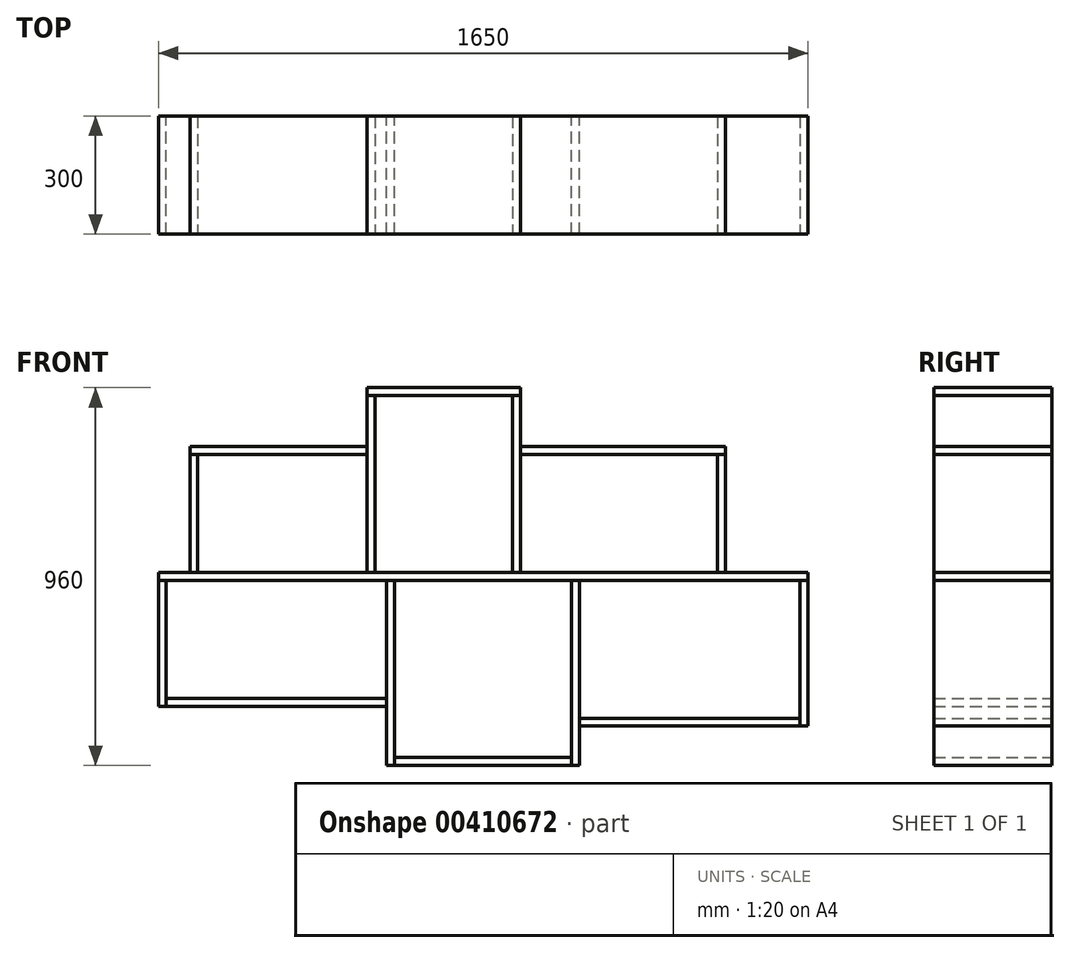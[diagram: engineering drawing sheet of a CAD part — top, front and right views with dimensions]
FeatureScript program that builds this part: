
annotation { "Feature Type Name" : "Feature", "Feature Type Description" : "" }
export const myFeature = defineFeature(function(context is Context, id is Id, definition is map)
    precondition{}
    {
        {
            var Q0;
            Q0=qCreatedBy(makeId("Top.planeOp"),FACE);
            var sketch = newSketch(context, id + "F0", { "sketchPlane" : qUnion([Q0])});
            skLineSegment(sketch, "E0.bottom", {"start": v(-825, 149.72) * mm, "end": v(825, 149.72) * mm});
            skLineSegment(sketch, "E0.top", {"start": v(-825, -150.28) * mm, "end": v(825, -150.28) * mm});
            skLineSegment(sketch, "E0.left", {"start": v(-825, 149.72) * mm, "end": v(-825, -150.28) * mm});
            skLineSegment(sketch, "E0.right", {"start": v(825, 149.72) * mm, "end": v(825, -150.28) * mm});
            skSolve(sketch);
        }
        {
            var Q0;
            Q0 = qSketchRegion(id + "F0", true);
            extrude(context, id + "F1", {"entities" : qUnion([Q0]), "depth" : 20 * mm});
        }
        {
            var Q0;
            Q0=makeQuery(id+"F1.opExtrude","CAP_FACE",FACE,{"disambiguationData":[OSD([sQuery(id+"F0.wireOp",EDGE,"E0.bottom"),sQuery(id+"F0.wireOp",EDGE,"E0.top"),sQuery(id+"F0.wireOp",EDGE,"E0.left"),sQuery(id+"F0.wireOp",EDGE,"E0.right")])],"isStart":false});
            var sketch = newSketch(context, id + "F2", { "sketchPlane" : qUnion([Q0])});
            skLineSegment(sketch, "E1.bottom", {"start": v(-725, 149.72) * mm, "end": v(-745, 149.72) * mm});
            skLineSegment(sketch, "E1.top", {"start": v(-725, -150.28) * mm, "end": v(-745, -150.28) * mm});
            skLineSegment(sketch, "E1.left", {"start": v(-745, 149.72) * mm, "end": v(-745, -150.28) * mm});
            skLineSegment(sketch, "E1.right", {"start": v(-725, 149.72) * mm, "end": v(-725, -150.28) * mm});
            skSolve(sketch);
        }
        {
            var Q0;
            Q0 = qSketchRegion(id + "F2", true);
            extrude(context, id + "F3", {"entities" : qUnion([Q0]), "depth" : 300 * mm});
        }
        {
            var Q0;
            Q0=makeQuery(id+"F1.opExtrude","CAP_FACE",FACE,{"disambiguationData":[OSD([sQuery(id+"F0.wireOp",EDGE,"E0.bottom"),sQuery(id+"F0.wireOp",EDGE,"E0.top"),sQuery(id+"F0.wireOp",EDGE,"E0.left"),sQuery(id+"F0.wireOp",EDGE,"E0.right")])],"isStart":false});
            var sketch = newSketch(context, id + "F4", { "sketchPlane" : qUnion([Q0])});
            skLineSegment(sketch, "E2.bottom", {"start": v(-295, 149.72) * mm, "end": v(-275, 149.72) * mm});
            skLineSegment(sketch, "E2.top", {"start": v(-295, -150.28) * mm, "end": v(-275, -150.28) * mm});
            skLineSegment(sketch, "E2.left", {"start": v(-295, 149.72) * mm, "end": v(-295, -150.28) * mm});
            skLineSegment(sketch, "E2.right", {"start": v(-275, 149.72) * mm, "end": v(-275, -150.28) * mm});
            skSolve(sketch);
        }
        {
            var Q0;
            Q0 = qSketchRegion(id + "F4", true);
            extrude(context, id + "F5", {"entities" : qUnion([Q0]), "depth" : 450 * mm});
        }
        {
            var Q0;
            Q0=makeQuery(id+"F1.opExtrude","CAP_FACE",FACE,{"disambiguationData":[OSD([sQuery(id+"F0.wireOp",EDGE,"E0.bottom"),sQuery(id+"F0.wireOp",EDGE,"E0.top"),sQuery(id+"F0.wireOp",EDGE,"E0.left"),sQuery(id+"F0.wireOp",EDGE,"E0.right")])],"isStart":false});
            var sketch = newSketch(context, id + "F6", { "sketchPlane" : qUnion([Q0])});
            skLineSegment(sketch, "E3.bottom", {"start": v(75, 149.72) * mm, "end": v(95, 149.72) * mm});
            skLineSegment(sketch, "E3.top", {"start": v(75, -150.28) * mm, "end": v(95, -150.28) * mm});
            skLineSegment(sketch, "E3.left", {"start": v(75, 149.72) * mm, "end": v(75, -150.28) * mm});
            skLineSegment(sketch, "E3.right", {"start": v(95, 149.72) * mm, "end": v(95, -150.28) * mm});
            skSolve(sketch);
        }
        {
            var Q0;
            Q0 = qSketchRegion(id + "F6", true);
            extrude(context, id + "F7", {"entities" : qUnion([Q0]), "depth" : 450 * mm});
        }
        {
            var Q0;
            Q0=makeQuery(id+"F1.opExtrude","CAP_FACE",FACE,{"disambiguationData":[OSD([sQuery(id+"F0.wireOp",EDGE,"E0.bottom"),sQuery(id+"F0.wireOp",EDGE,"E0.top"),sQuery(id+"F0.wireOp",EDGE,"E0.left"),sQuery(id+"F0.wireOp",EDGE,"E0.right")])],"isStart":false});
            var sketch = newSketch(context, id + "F8", { "sketchPlane" : qUnion([Q0])});
            skLineSegment(sketch, "E4.bottom", {"start": v(595, 149.72) * mm, "end": v(615, 149.72) * mm});
            skLineSegment(sketch, "E4.top", {"start": v(595, -150.28) * mm, "end": v(615, -150.28) * mm});
            skLineSegment(sketch, "E4.left", {"start": v(595, 149.72) * mm, "end": v(595, -150.28) * mm});
            skLineSegment(sketch, "E4.right", {"start": v(615, 149.72) * mm, "end": v(615, -150.28) * mm});
            skSolve(sketch);
        }
        {
            var Q0;
            Q0 = qSketchRegion(id + "F8", true);
            extrude(context, id + "F9", {"entities" : qUnion([Q0]), "depth" : 300 * mm});
        }
        {
            var Q0;
            Q0=makeQuery(id+"F3.opExtrude","CAP_FACE",FACE,{"disambiguationData":[OSD([sQuery(id+"F2.wireOp",EDGE,"E1.bottom"),sQuery(id+"F2.wireOp",EDGE,"E1.top"),sQuery(id+"F2.wireOp",EDGE,"E1.left"),sQuery(id+"F2.wireOp",EDGE,"E1.right")])],"isStart":false});
            var sketch = newSketch(context, id + "F10", { "sketchPlane" : qUnion([Q0])});
            skLineSegment(sketch, "E5.bottom", {"start": v(-745, 149.72) * mm, "end": v(-295, 149.72) * mm});
            skLineSegment(sketch, "E5.top", {"start": v(-745, -150.28) * mm, "end": v(-295, -150.28) * mm});
            skLineSegment(sketch, "E5.left", {"start": v(-745, 149.72) * mm, "end": v(-745, -150.28) * mm});
            skLineSegment(sketch, "E5.right", {"start": v(-295, 149.72) * mm, "end": v(-295, -150.28) * mm});
            skSolve(sketch);
        }
        {
            var Q0;
            Q0 = qSketchRegion(id + "F10", true);
            extrude(context, id + "F11", {"entities" : qUnion([Q0]), "depth" : 20 * mm});
        }
        {
            var Q0;
            Q0=makeQuery(id+"F5.opExtrude","CAP_FACE",FACE,{"disambiguationData":[OSD([sQuery(id+"F4.wireOp",EDGE,"E2.bottom"),sQuery(id+"F4.wireOp",EDGE,"E2.top"),sQuery(id+"F4.wireOp",EDGE,"E2.left"),sQuery(id+"F4.wireOp",EDGE,"E2.right")])],"isStart":false});
            var sketch = newSketch(context, id + "F12", { "sketchPlane" : qUnion([Q0])});
            skLineSegment(sketch, "E6.bottom", {"start": v(-295, 149.72) * mm, "end": v(95, 149.72) * mm});
            skLineSegment(sketch, "E6.top", {"start": v(-295, -150.28) * mm, "end": v(95, -150.28) * mm});
            skLineSegment(sketch, "E6.left", {"start": v(-295, 149.72) * mm, "end": v(-295, -150.28) * mm});
            skLineSegment(sketch, "E6.right", {"start": v(95, 149.72) * mm, "end": v(95, -150.28) * mm});
            skSolve(sketch);
        }
        {
            var Q0;
            Q0 = qSketchRegion(id + "F12", true);
            extrude(context, id + "F13", {"entities" : qUnion([Q0]), "depth" : 20 * mm});
        }
        {
            var Q0;
            Q0=makeQuery(id+"F9.opExtrude","CAP_FACE",FACE,{"disambiguationData":[OSD([sQuery(id+"F8.wireOp",EDGE,"E4.bottom"),sQuery(id+"F8.wireOp",EDGE,"E4.top"),sQuery(id+"F8.wireOp",EDGE,"E4.left"),sQuery(id+"F8.wireOp",EDGE,"E4.right")])],"isStart":false});
            var sketch = newSketch(context, id + "F14", { "sketchPlane" : qUnion([Q0])});
            skLineSegment(sketch, "E7.bottom", {"start": v(615, -150.28) * mm, "end": v(95, -150.28) * mm});
            skLineSegment(sketch, "E7.top", {"start": v(615, 149.72) * mm, "end": v(95, 149.72) * mm});
            skLineSegment(sketch, "E7.left", {"start": v(615, -150.28) * mm, "end": v(615, 149.72) * mm});
            skLineSegment(sketch, "E7.right", {"start": v(95, -150.28) * mm, "end": v(95, 149.72) * mm});
            skSolve(sketch);
        }
        {
            var Q0;
            Q0 = qSketchRegion(id + "F14", true);
            extrude(context, id + "F15", {"entities" : qUnion([Q0]), "depth" : 20 * mm});
        }
        {
            var Q0;
            Q0=makeQuery(id+"F1.opExtrude","CAP_FACE",FACE,{"disambiguationData":[OSD([sQuery(id+"F0.wireOp",EDGE,"E0.bottom"),sQuery(id+"F0.wireOp",EDGE,"E0.top"),sQuery(id+"F0.wireOp",EDGE,"E0.left"),sQuery(id+"F0.wireOp",EDGE,"E0.right")])],"isStart":true});
            var sketch = newSketch(context, id + "F16", { "sketchPlane" : qUnion([Q0])});
            skLineSegment(sketch, "E8.bottom", {"start": v(-825, 150.28) * mm, "end": v(-805, 150.28) * mm});
            skLineSegment(sketch, "E8.top", {"start": v(-825, -149.72) * mm, "end": v(-805, -149.72) * mm});
            skLineSegment(sketch, "E8.left", {"start": v(-825, 150.28) * mm, "end": v(-825, -149.72) * mm});
            skLineSegment(sketch, "E8.right", {"start": v(-805, 150.28) * mm, "end": v(-805, -149.72) * mm});
            skSolve(sketch);
        }
        {
            var Q0;
            Q0 = qSketchRegion(id + "F16", true);
            extrude(context, id + "F17", {"entities" : qUnion([Q0]), "depth" : 320 * mm});
        }
        {
            var Q0;
            Q0=makeQuery(id+"F1.opExtrude","CAP_FACE",FACE,{"disambiguationData":[OSD([sQuery(id+"F0.wireOp",EDGE,"E0.bottom"),sQuery(id+"F0.wireOp",EDGE,"E0.top"),sQuery(id+"F0.wireOp",EDGE,"E0.left"),sQuery(id+"F0.wireOp",EDGE,"E0.right")])],"isStart":true});
            var sketch = newSketch(context, id + "F18", { "sketchPlane" : qUnion([Q0])});
            skLineSegment(sketch, "E9.bottom", {"start": v(-245, 150.28) * mm, "end": v(-225, 150.28) * mm});
            skLineSegment(sketch, "E9.top", {"start": v(-245, -149.72) * mm, "end": v(-225, -149.72) * mm});
            skLineSegment(sketch, "E9.left", {"start": v(-245, 150.28) * mm, "end": v(-245, -149.72) * mm});
            skLineSegment(sketch, "E9.right", {"start": v(-225, 150.28) * mm, "end": v(-225, -149.72) * mm});
            skSolve(sketch);
        }
        {
            var Q0;
            Q0 = qSketchRegion(id + "F18", true);
            extrude(context, id + "F19", {"entities" : qUnion([Q0]), "depth" : 470 * mm});
        }
        {
            var Q0;
            Q0=makeQuery(id+"F1.opExtrude","CAP_FACE",FACE,{"disambiguationData":[OSD([sQuery(id+"F0.wireOp",EDGE,"E0.bottom"),sQuery(id+"F0.wireOp",EDGE,"E0.top"),sQuery(id+"F0.wireOp",EDGE,"E0.left"),sQuery(id+"F0.wireOp",EDGE,"E0.right")])],"isStart":true});
            var sketch = newSketch(context, id + "F20", { "sketchPlane" : qUnion([Q0])});
            skLineSegment(sketch, "E10.bottom", {"start": v(245, 150.28) * mm, "end": v(225, 150.28) * mm});
            skLineSegment(sketch, "E10.top", {"start": v(245, -149.72) * mm, "end": v(225, -149.72) * mm});
            skLineSegment(sketch, "E10.left", {"start": v(245, 150.28) * mm, "end": v(245, -149.72) * mm});
            skLineSegment(sketch, "E10.right", {"start": v(225, 150.28) * mm, "end": v(225, -149.72) * mm});
            skSolve(sketch);
        }
        {
            var Q0;
            Q0 = qSketchRegion(id + "F20", true);
            extrude(context, id + "F21", {"entities" : qUnion([Q0]), "depth" : 470 * mm});
        }
        {
            var Q0;
            Q0=makeQuery(id+"F1.opExtrude","CAP_FACE",FACE,{"disambiguationData":[OSD([sQuery(id+"F0.wireOp",EDGE,"E0.bottom"),sQuery(id+"F0.wireOp",EDGE,"E0.top"),sQuery(id+"F0.wireOp",EDGE,"E0.left"),sQuery(id+"F0.wireOp",EDGE,"E0.right")])],"isStart":true});
            var sketch = newSketch(context, id + "F22", { "sketchPlane" : qUnion([Q0])});
            skLineSegment(sketch, "E11.bottom", {"start": v(825, 150.28) * mm, "end": v(805, 150.28) * mm});
            skLineSegment(sketch, "E11.top", {"start": v(825, -149.72) * mm, "end": v(805, -149.72) * mm});
            skLineSegment(sketch, "E11.left", {"start": v(825, 150.28) * mm, "end": v(825, -149.72) * mm});
            skLineSegment(sketch, "E11.right", {"start": v(805, 150.28) * mm, "end": v(805, -149.72) * mm});
            skSolve(sketch);
        }
        {
            var Q0;
            Q0 = qSketchRegion(id + "F22", true);
            extrude(context, id + "F23", {"entities" : qUnion([Q0]), "depth" : 370 * mm});
        }
        {
            var Q0;
            Q0=makeQuery(id+"F17.opExtrude","SWEPT_FACE",FACE,{"disambiguationData":[OSD([sQuery(id+"F16.wireOp",EDGE,"E8.right")])]});
            var sketch = newSketch(context, id + "F24", { "sketchPlane" : qUnion([Q0])});
            skLineSegment(sketch, "E12.bottom", {"start": v(-150.28, -320) * mm, "end": v(149.72, -320) * mm});
            skLineSegment(sketch, "E12.top", {"start": v(-150.28, -300) * mm, "end": v(149.72, -300) * mm});
            skLineSegment(sketch, "E12.left", {"start": v(-150.28, -320) * mm, "end": v(-150.28, -300) * mm});
            skLineSegment(sketch, "E12.right", {"start": v(149.72, -320) * mm, "end": v(149.72, -300) * mm});
            skSolve(sketch);
        }
        {
            var Q0;
            Q0 = qSketchRegion(id + "F24", true);
            extrude(context, id + "F25", {"entities" : qUnion([Q0]), "endBound" : BoundingType.UP_TO_NEXT, "depth" : 25 * mm});
        }
        {
            var Q0;
            Q0=makeQuery(id+"F19.opExtrude","SWEPT_FACE",FACE,{"disambiguationData":[OSD([sQuery(id+"F18.wireOp",EDGE,"E9.right")])]});
            var sketch = newSketch(context, id + "F26", { "sketchPlane" : qUnion([Q0])});
            skLineSegment(sketch, "E13.bottom", {"start": v(-150.28, -470) * mm, "end": v(149.72, -470) * mm});
            skLineSegment(sketch, "E13.top", {"start": v(-150.28, -450) * mm, "end": v(149.72, -450) * mm});
            skLineSegment(sketch, "E13.left", {"start": v(-150.28, -470) * mm, "end": v(-150.28, -450) * mm});
            skLineSegment(sketch, "E13.right", {"start": v(149.72, -470) * mm, "end": v(149.72, -450) * mm});
            skSolve(sketch);
        }
        {
            var Q0;
            Q0 = qSketchRegion(id + "F26", true);
            extrude(context, id + "F27", {"entities" : qUnion([Q0]), "endBound" : BoundingType.UP_TO_NEXT, "depth" : 25 * mm});
        }
        {
            var Q0;
            Q0=makeQuery(id+"F23.opExtrude","SWEPT_FACE",FACE,{"disambiguationData":[OSD([sQuery(id+"F22.wireOp",EDGE,"E11.right")])]});
            var sketch = newSketch(context, id + "F28", { "sketchPlane" : qUnion([Q0])});
            skLineSegment(sketch, "E14.bottom", {"start": v(-149.72, -370) * mm, "end": v(150.28, -370) * mm});
            skLineSegment(sketch, "E14.top", {"start": v(-149.72, -350) * mm, "end": v(150.28, -350) * mm});
            skLineSegment(sketch, "E14.left", {"start": v(-149.72, -370) * mm, "end": v(-149.72, -350) * mm});
            skLineSegment(sketch, "E14.right", {"start": v(150.28, -370) * mm, "end": v(150.28, -350) * mm});
            skSolve(sketch);
        }
        {
            var Q0;
            Q0 = qSketchRegion(id + "F28", true);
            extrude(context, id + "F29", {"entities" : qUnion([Q0]), "endBound" : BoundingType.UP_TO_NEXT, "depth" : 25 * mm});
        }
    });
